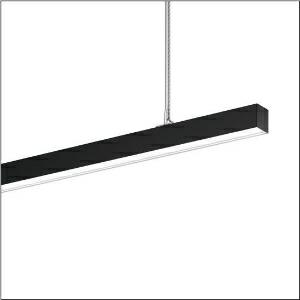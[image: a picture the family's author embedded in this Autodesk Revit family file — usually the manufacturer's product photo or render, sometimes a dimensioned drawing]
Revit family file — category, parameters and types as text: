
# Revit family: silica_r__21_51mx30db45bb_77a6
name_source: partatom
category: Lighting Fixtures
units: mm (PartAtom-declared; Revit-internal decimal feet)

## family parameters
Cut with Voids When Loaded = No
Host = Face
Light Source = No
Part Type = Normal
Room Calculation Point = No
Round Connector Dimension = Use Diameter
Shared = No

## types (1)
- --- (1 x LED, 5260 lm, 32 W, 4000K)
    Apparent Load = 32 VA
    CIE Flux Codes = 47 79 96 57 100
    Color Rendering = 80
    Color Temperature = 4000K
    Default Elevation = 1800 mm
    Description = Silica® 21, office luminaire, primary optical cover: cover, of PMMA, opal, light emission: direct/indirect distribution, primary light characteristic: symmetric, installation type: suspended mounting, LED, rated luminous flux: 5.260lm, luminous efficacy: 164lm/W, light colour: 840, colour temperature: 4000K, control gear: DALI 2, with terminal, 3+2-pole, max. 2.5mm², mains connection: 220..240V, AC, 50/60Hz, rated input power: 32W, luminaire housing, of aluminium, matt jet black (RAL 9005), length: 1.504mm, width: 53mm, height: 53mm, protection rating (complete): IP20, insulation class (complete): insulation class I (protective earthing), certification: CE, permissible operating ambient temperature: 0..+35°C, standard: EN 50419, packaging unit: 1 piece
    Height = 53 mm
    Lamp = 1 x LED
    Lamp Light Flux = 5260 lm
    Lamp Power = 32 W
    Lamp count = 1
    Length = 1504 mm
    Luminous efficacy = 164 lm/W
    Manufacturer = Siteco
    ModVariant = No
    Model = 51MX30DB45BB
    Mounting Place = Ceiling
    Mounting Type = Pendant
    Number of Poles = 1
    OnlyDefault = Yes
    Power Factor = 1
    Product Name = Silica® 21
    Product group = office luminaire | ceiling pendant
    ProductGroupID = 904
    Protection Class = Protection class I
    Protection Degree = IP 20
    RLX_Detail_Level = 1
    RLX_Emergency_Light_Flux = 0 lm
    RLX_Emergency_Type = 0
    RLX_Emergency_Type_DB = No
    RlxData = <blob elided: 26025 chars, md5=513940d9>
    Socket = socket
    Standby Power = 0 W
    System Light Flux = 5260 lm
    System Power = 32 W
    Type Comments = factory setting: luminous flux: 100 % | dim-lin: 254 | 218 mA
    Type Image = l_1335856.jpg
    URL = http://relux.com
    VarID = @adj_117020
    Voltage = 0 V
    Weight = 0.00 kg
    Width = 53 mm

## geometry (parser evidence)
native form markers: Blend x4, Sweep x12
no freeform markers — native parametric forms only
